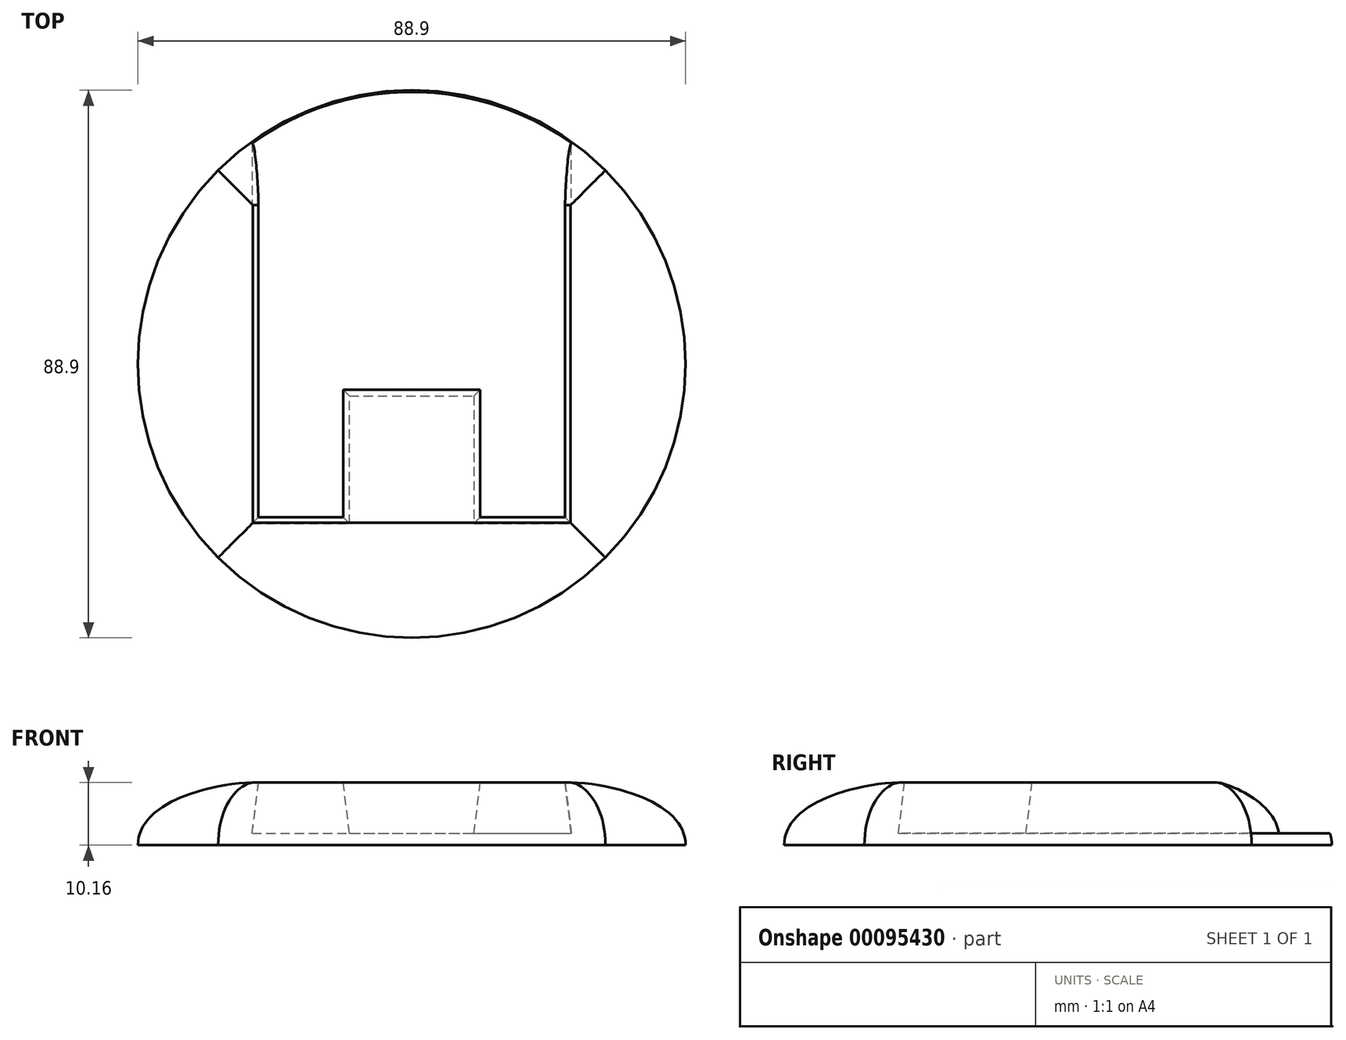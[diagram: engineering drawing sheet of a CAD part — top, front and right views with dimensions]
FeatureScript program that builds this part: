
annotation { "Feature Type Name" : "Feature", "Feature Type Description" : "" }
export const myFeature = defineFeature(function(context is Context, id is Id, definition is map)
    precondition{}
    {
        {
            var Q0;
            Q0=qCreatedBy(makeId("Top.planeOp"),FACE);
            var sketch = newSketch(context, id + "F0", { "sketchPlane" : qUnion([Q0])});
            skCircle(sketch, "E0", {"center": v(0, 0) * mm, "radius": 44.45 * mm});
            skSolve(sketch);
        }
        {
            var Q0;
            Q0=qCreatedBy(makeId("Top.planeOp"),FACE);
            cPlane(context, id + "F1", {"entities" : qUnion([Q0]), "cplaneType" : CPlaneType.OFFSET, "offset" : 10.16 * mm, "width" : 152.4 * mm, "height" : 152.4 * mm});
        }
        {
            var Q0;
            Q0=qCreatedBy(id+"F1.planeOp",FACE);
            var sketch = newSketch(context, id + "F2", { "sketchPlane" : qUnion([Q0])});
            skLineSegment(sketch, "E1.bottom", {"start": v(25.78, -25.78) * mm, "end": v(-25.78, -25.78) * mm});
            skLineSegment(sketch, "E1.top", {"start": v(25.78, 25.78) * mm, "end": v(-25.78, 25.78) * mm});
            skLineSegment(sketch, "E1.left", {"start": v(25.78, -25.78) * mm, "end": v(25.78, 25.78) * mm});
            skLineSegment(sketch, "E1.right", {"start": v(-25.78, -25.78) * mm, "end": v(-25.78, 25.78) * mm});
            skPoint(sketch, "E1.middle", {"position": v(0, 0) * mm});
            skSolve(sketch);
        }
        {
            var Q0;
            Q0 = qSketchRegion(id + "F0", true);
            var Q1;
            Q1 = qSketchRegion(id + "F2", true);
            loft(context, id + "F3", {"startCondition" : LoftEndDerivativeType.NORMAL_TO_PROFILE, "startMagnitude" : 2, "endCondition" : LoftEndDerivativeType.TANGENT_TO_PROFILE, "endMagnitude" : 1, "sheetProfilesArray" : [{ "sheetProfileEntities" : qUnion([Q0]) }, { "sheetProfileEntities" : qUnion([Q1]) }]});
        }
        {
            var Q0;
            Q0=makeQuery(id+"F2.imprint","IMPRINT",FACE,{"disambiguationData":[TD([[makeQuery(id+"F2.imprint","IMPRINT",EDGE,{"derivedFrom":sQuery(id+"F2.wireOp",EDGE,"E1.bottom")}),-1.0]])]});
            var sketch = newSketch(context, id + "F4", { "sketchPlane" : qUnion([Q0])});
            skLineSegment(sketch, "E2.0", {"start": v(-24.9, -24.9) * mm, "end": v(-11.11, -24.9) * mm});
            skLineSegment(sketch, "E2.1", {"start": v(-24.9, 63.72) * mm, "end": v(-24.9, -24.9) * mm});
            skLineSegment(sketch, "E2.2", {"start": v(24.9, 63.72) * mm, "end": v(-24.9, 63.72) * mm});
            skLineSegment(sketch, "E2.3", {"start": v(24.9, -24.9) * mm, "end": v(24.9, 63.72) * mm});
            skLineSegment(sketch, "E3", {"start": v(-11.11, -24.9) * mm, "end": v(-11.11, -4.2) * mm});
            skLineSegment(sketch, "E4", {"start": v(-11.11, -4.2) * mm, "end": v(11.11, -4.2) * mm});
            skLineSegment(sketch, "E5", {"start": v(11.11, -4.2) * mm, "end": v(11.11, -24.9) * mm});
            skLineSegment(sketch, "E6.trimOffspring", {"start": v(11.11, -24.9) * mm, "end": v(24.9, -24.9) * mm});
            skSolve(sketch);
        }
        {
            var Q0;
            Q0 = qSketchRegion(id + "F4", true);
            extrude(context, id + "F5", {"entities" : qUnion([Q0]), "operationType" : NewBodyOperationType.REMOVE, "oppositeDirection" : true, "depth" : 8.25 * mm, "hasDraft" : true, "draftAngle" : 7 * degree});
        }
    });
